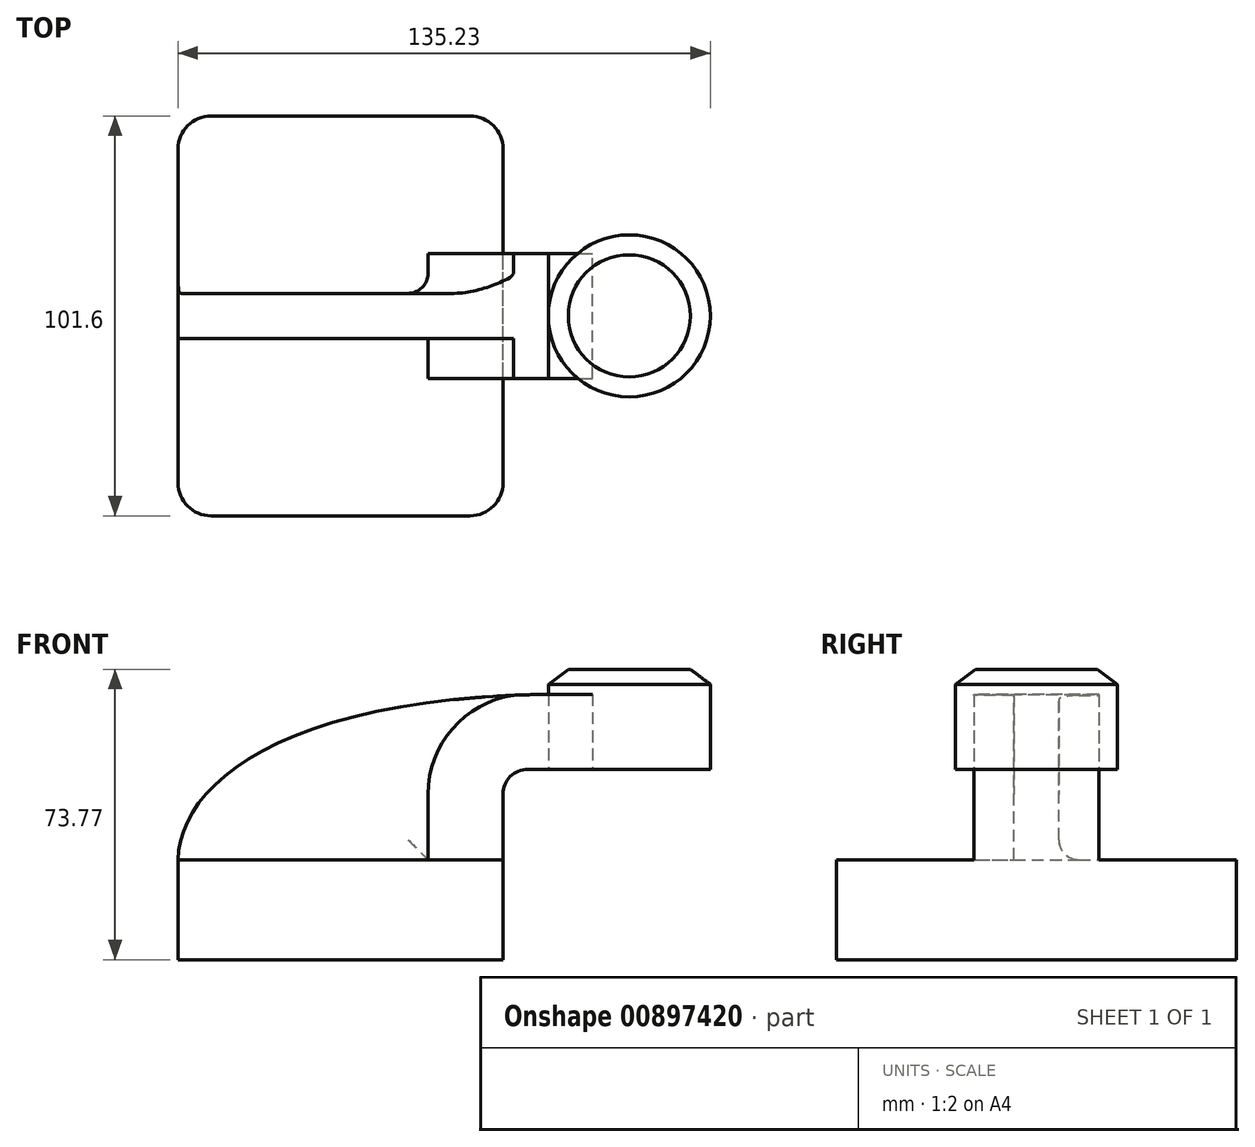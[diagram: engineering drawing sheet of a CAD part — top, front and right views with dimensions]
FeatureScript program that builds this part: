
annotation { "Feature Type Name" : "Feature", "Feature Type Description" : "" }
export const myFeature = defineFeature(function(context is Context, id is Id, definition is map)
    precondition{}
    {
        {
            var Q0;
            Q0=qCreatedBy(makeId("Front.planeOp"),FACE);
            var sketch = newSketch(context, id + "F0", { "sketchPlane" : qUnion([Q0])});
            skLineSegment(sketch, "E0.bottom", {"start": v(41.27, 12.7) * mm, "end": v(-41.28, 12.7) * mm});
            skLineSegment(sketch, "E0.top", {"start": v(41.28, -12.7) * mm, "end": v(-41.27, -12.7) * mm});
            skLineSegment(sketch, "E0.left", {"start": v(41.28, 12.7) * mm, "end": v(41.28, -12.7) * mm});
            skLineSegment(sketch, "E0.right", {"start": v(-41.28, 12.7) * mm, "end": v(-41.27, -12.7) * mm});
            skPoint(sketch, "E0.middle", {"position": v(0, 0) * mm});
            skLineSegment(sketch, "E1.bottom", {"start": v(93.95, 35.67) * mm, "end": v(52.8, 35.67) * mm});
            skLineSegment(sketch, "E1.top", {"start": v(93.95, 61.07) * mm, "end": v(52.8, 61.07) * mm});
            skLineSegment(sketch, "E1.left", {"start": v(93.95, 35.67) * mm, "end": v(93.95, 61.07) * mm});
            skLineSegment(sketch, "E1.right", {"start": v(52.8, 35.67) * mm, "end": v(52.8, 61.07) * mm});
            skPoint(sketch, "E1.middle", {"position": v(73.37, 48.37) * mm});
            skLineSegment(sketch, "E2", {"start": v(41.27, 12.7) * mm, "end": v(41.27, 29.33) * mm});
            skArc(sketch, "E3", {"start": v(41.27, 29.33) * mm, "mid": v(43.13, 33.81) * mm, "end": v(47.6, 35.67) * mm});
            skLineSegment(sketch, "E4", {"start": v(47.6, 35.67) * mm, "end": v(64.02, 35.67) * mm});
            skLineSegment(sketch, "E5.0", {"start": v(47.6, 54.72) * mm, "end": v(64.02, 54.72) * mm});
            skArc(sketch, "E5.1", {"start": v(22.22, 29.33) * mm, "mid": v(29.66, 47.28) * mm, "end": v(47.6, 54.72) * mm});
            skLineSegment(sketch, "E5.2", {"start": v(22.22, 12.7) * mm, "end": v(22.22, 29.33) * mm});
            skLineSegment(sketch, "E6", {"start": v(64.02, 54.72) * mm, "end": v(64.02, 35.67) * mm});
            skLineSegment(sketch, "E7", {"start": v(22.22, 12.7) * mm, "end": v(41.27, 12.7) * mm});
            skFitSpline(sketch, "E8", {"points": [v(-41.28, 12.7) * mm, v(52.8, 54.72) * mm], "startDerivative": vector(1.42, 56.9) * mm, "endDerivative": vector(204.59, 3.17) * mm});
            skLineSegment(sketch, "E9", {"start": v(73.37, 35.67) * mm, "end": v(73.37, 61.07) * mm});
            skSolve(sketch);
        }
        {
            var Q0;
            Q0=makeQuery(id+"F0.imprint","IMPRINT",FACE,{"disambiguationData":[TD([[makeQuery(id+"F0.imprint","IMPRINT",EDGE,{"derivedFrom":sQuery(id+"F0.wireOp",EDGE,"E0.bottom")}),1.0]])]});
            extrude(context, id + "F1", {"entities" : qUnion([Q0]), "endBound" : BoundingType.SYMMETRIC, "depth" : 101.6 * mm, "offsetDistance" : 25.4 * mm});
        }
        {
            var Q0;
            Q0=makeQuery(id+"F0.imprint","IMPRINT",FACE,{"disambiguationData":[TD([[makeQuery(id+"F0.imprint","IMPRINT",EDGE,{"derivedFrom":sQuery(id+"F0.wireOp",EDGE,"E2")}),1.0]])]});
            var Q1;
            {var subQ5=sQuery(id+"F0.wireOp",EDGE,"E6");Q1=makeQuery(id+"F0.imprint","IMPRINT",FACE,{"disambiguationData":[TD([[makeQuery(id+"F0.imprint","IMPRINT",EDGE,{"derivedFrom":subQ5}),-1.0]])]});}
            extrude(context, id + "F2", {"entities" : qUnion([Q0, Q1]), "operationType" : NewBodyOperationType.ADD, "endBound" : BoundingType.SYMMETRIC, "depth" : 31.75 * mm, "offsetDistance" : 25.4 * mm});
        }
        {
            var Q0;
            {var subQ0=sQuery(id+"F0.wireOp",EDGE,"E0.bottom");Q0=makeQuery(id+"F0.imprint","IMPRINT",FACE,{"disambiguationData":[TD([[makeQuery(id+"F0.imprint","IMPRINT",EDGE,{"derivedFrom":subQ0}),-1.0]])]});}
            extrude(context, id + "F3", {"entities" : qUnion([Q0]), "operationType" : NewBodyOperationType.ADD, "endBound" : BoundingType.SYMMETRIC, "depth" : 11.43 * mm, "offsetDistance" : 25.4 * mm});
        }
        {
            var Q0;
            {var subQ0=sQuery(id+"F0.wireOp",EDGE,"E1.left");Q0=makeQuery(id+"F0.imprint","IMPRINT",FACE,{"disambiguationData":[TD([[makeQuery(id+"F0.imprint","IMPRINT",EDGE,{"derivedFrom":subQ0}),1.0]])]});}
            var Q1;
            Q1=sQuery(id+"F0.wireOp",EDGE,"E9");
            revolve(context, id + "F4", {"surfaceOperationType" : NewSurfaceOperationType.NEW, "entities" : qUnion([Q0]), "axis" : qUnion([Q1]), "revolveType" : RevolveType.FULL});
        }
        {
            var Q0;
            Q0=makeQuery(id+"F1.opExtrude","CAP_EDGE",EDGE,{"disambiguationData":[OSD([sQuery(id+"F0.wireOp",EDGE,"E0.right")])],"isStart":false});
            var Q1;
            Q1=makeQuery(id+"F1.opExtrude","CAP_EDGE",EDGE,{"disambiguationData":[OSD([sQuery(id+"F0.wireOp",EDGE,"E0.left")])],"isStart":false});
            var Q2;
            Q2=makeQuery(id+"F1.opExtrude","CAP_EDGE",EDGE,{"disambiguationData":[OSD([sQuery(id+"F0.wireOp",EDGE,"E0.left")])],"isStart":true});
            var Q3;
            Q3=makeQuery(id+"F1.opExtrude","CAP_EDGE",EDGE,{"disambiguationData":[OSD([sQuery(id+"F0.wireOp",EDGE,"E0.right")])],"isStart":true});
            fillet(context, id + "F5", {"entities" : qUnion([Q0, Q1, Q2, Q3]), "radius" : 8.38 * mm, "tangentPropagation" : true, "allowEdgeOverflow" : false});
        }
        {
            var Q0;
            Q0=makeQuery(id+"F4.opRevolve","SWEPT_EDGE",EDGE,{"disambiguationData":[OSD([sQuery(id+"F0.wireOp",EDGE,"E1.top"),sQuery(id+"F0.wireOp",EDGE,"E1.left")])]});
            chamfer(context, id + "F6", {"entities" : qUnion([Q0]), "chamferType" : ChamferType.TWO_OFFSETS, "width1" : 5.08 * mm, "oppositeDirection" : true, "width2" : 3.8 * mm, "tangentPropagation" : true});
        }
        {
            var Q0;
            Q0=makeQuery(id+"F3.opExtrude","CAP_EDGE",EDGE,{"disambiguationData":[OSD([sQuery(id+"F0.wireOp",EDGE,"E0.bottom")])],"isStart":false});
            var Q1;
            Q1=makeQuery(id+"F3.opExtrude","CAP_EDGE",EDGE,{"disambiguationData":[OSD([sQuery(id+"F0.wireOp",EDGE,"E5.2")])],"isStart":false});
            var Q2;
            {var subQ0=sQuery(id+"F0.wireOp",EDGE,"E7");var subQ1=sQuery(id+"F0.wireOp",EDGE,"E0.bottom");var subQ2=sQuery(id+"F0.wireOp",EDGE,"E8");var subQ3=sQuery(id+"F0.wireOp",EDGE,"E5.2");var subQ4=sQuery(id+"F0.wireOp",EDGE,"E5.1");Q2=makeQuery(id+"F3.boolean.opBoolean","SPLIT",EDGE,{"disambiguationData":[TD([makeQuery(id+"F3.opExtrude","CAP_FACE",FACE,{"disambiguationData":[OSD([subQ1,subQ4,subQ3,subQ2])],"isStart":false})])],"derivedFrom":makeQuery(id+"F2.opExtrude","SWEPT_EDGE",EDGE,{"disambiguationData":[OSD([subQ1,subQ3,subQ0])]})});}
            var Q3;
            Q3=makeQuery(id+"F2.opExtrude","CAP_EDGE",EDGE,{"disambiguationData":[OSD([sQuery(id+"F0.wireOp",EDGE,"E7")])],"isStart":false});
            var Q4;
            Q4=makeQuery(id+"F3.opExtrude","CAP_EDGE",EDGE,{"disambiguationData":[OSD([sQuery(id+"F0.wireOp",EDGE,"E5.1")])],"isStart":false});
            var Q5;
            Q5=makeQuery(id+"F3.opExtrude","CAP_EDGE",EDGE,{"disambiguationData":[OSD([sQuery(id+"F0.wireOp",EDGE,"E5.2")])],"isStart":true});
            var Q6;
            Q6=makeQuery(id+"F3.opExtrude","CAP_EDGE",EDGE,{"disambiguationData":[OSD([sQuery(id+"F0.wireOp",EDGE,"E0.bottom")])],"isStart":true});
            var Q7;
            Q7=makeQuery(id+"F3.opExtrude","CAP_EDGE",EDGE,{"disambiguationData":[OSD([sQuery(id+"F0.wireOp",EDGE,"E5.1")])],"isStart":true});
            var Q8;
            Q8=makeQuery(id+"F2.opExtrude","CAP_EDGE",EDGE,{"disambiguationData":[OSD([sQuery(id+"F0.wireOp",EDGE,"E7")])],"isStart":true});
            var Q9;
            {var subQ0=sQuery(id+"F0.wireOp",EDGE,"E7");var subQ1=sQuery(id+"F0.wireOp",EDGE,"E0.bottom");var subQ2=sQuery(id+"F0.wireOp",EDGE,"E8");var subQ3=sQuery(id+"F0.wireOp",EDGE,"E5.2");var subQ4=sQuery(id+"F0.wireOp",EDGE,"E5.1");Q9=makeQuery(id+"F3.boolean.opBoolean","SPLIT",EDGE,{"disambiguationData":[TD([makeQuery(id+"F3.opExtrude","CAP_FACE",FACE,{"disambiguationData":[OSD([subQ1,subQ4,subQ3,subQ2])],"isStart":true})])],"derivedFrom":makeQuery(id+"F2.opExtrude","SWEPT_EDGE",EDGE,{"disambiguationData":[OSD([subQ1,subQ3,subQ0])]})});}
            fillet(context, id + "F7", {"entities" : qUnion([Q0, Q1, Q2, Q3, Q4, Q5, Q6, Q7, Q8, Q9]), "radius" : 5.08 * mm, "tangentPropagation" : true, "allowEdgeOverflow" : false});
        }
    });
